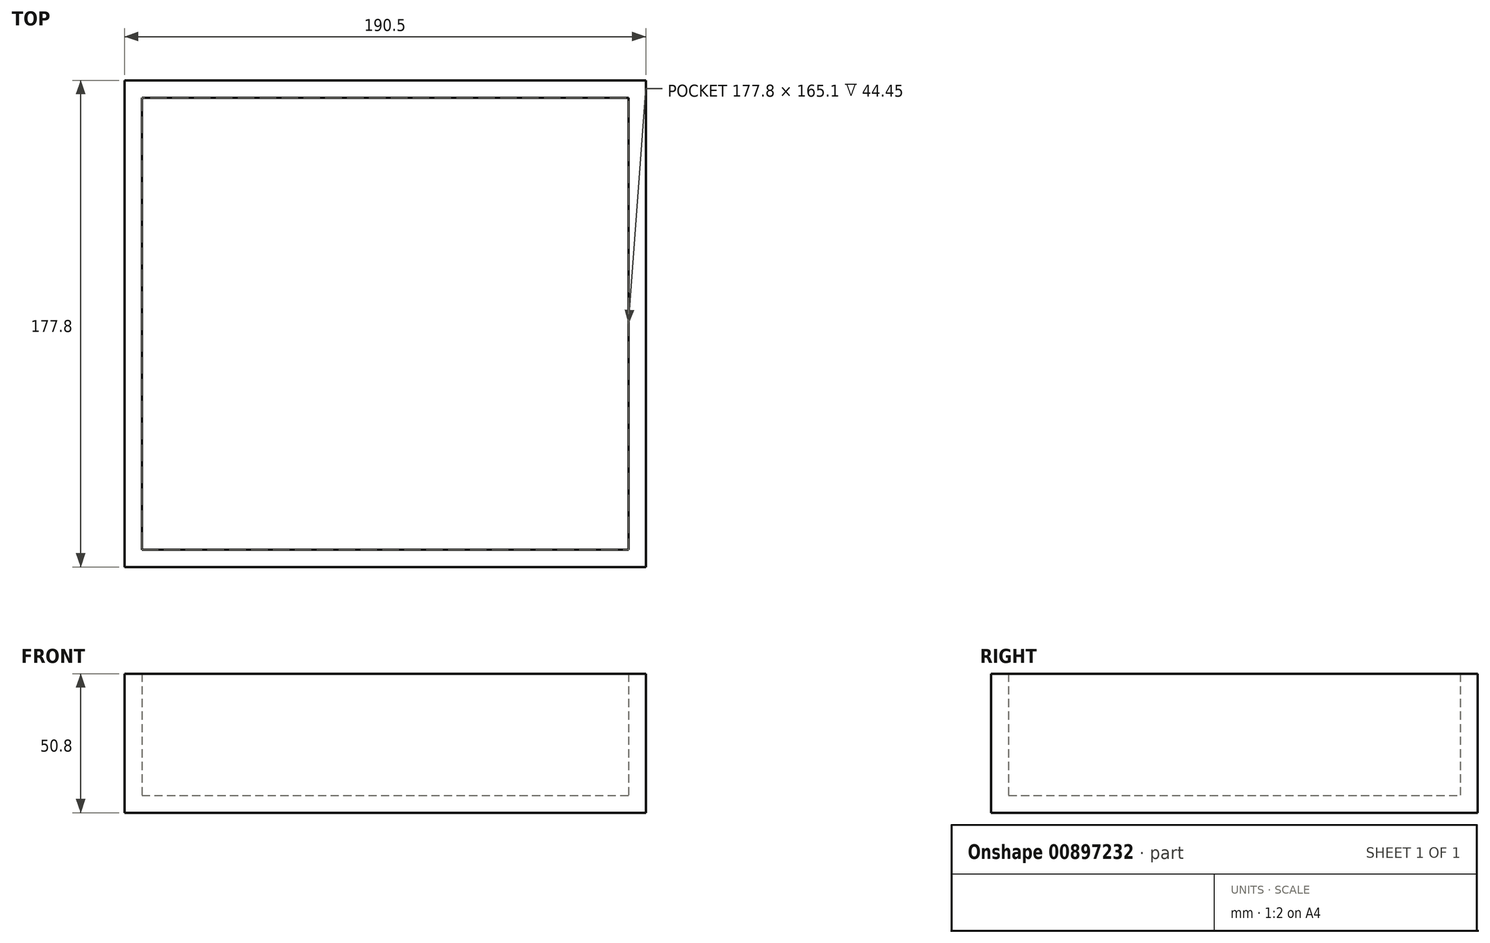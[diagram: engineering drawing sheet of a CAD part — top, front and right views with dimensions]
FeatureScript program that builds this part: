
annotation { "Feature Type Name" : "Feature", "Feature Type Description" : "" }
export const myFeature = defineFeature(function(context is Context, id is Id, definition is map)
    precondition{}
    {
        {
            var Q0;
            Q0=qCreatedBy(makeId("Top.planeOp"),FACE);
            var sketch = newSketch(context, id + "F0", { "sketchPlane" : qUnion([Q0])});
            skLineSegment(sketch, "E0.bottom", {"start": v(-88.9, -82.55) * mm, "end": v(88.9, -82.55) * mm});
            skLineSegment(sketch, "E0.top", {"start": v(-88.9, 82.55) * mm, "end": v(88.9, 82.55) * mm});
            skLineSegment(sketch, "E0.left", {"start": v(-88.9, -82.55) * mm, "end": v(-88.9, 82.55) * mm});
            skLineSegment(sketch, "E0.right", {"start": v(88.9, -82.55) * mm, "end": v(88.9, 82.55) * mm});
            skSolve(sketch);
        }
        {
            var Q0;
            Q0 = qSketchRegion(id + "F0", true);
            extrude(context, id + "F1", {"entities" : qUnion([Q0]), "depth" : 6.35 * mm, "offsetDistance" : 25.4 * mm});
        }
        {
            var Q0;
            Q0=qCreatedBy(makeId("Top.planeOp"),FACE);
            var sketch = newSketch(context, id + "F2", { "sketchPlane" : qUnion([Q0])});
            skLineSegment(sketch, "E1.bottom", {"start": v(-95.25, 88.9) * mm, "end": v(95.25, 88.9) * mm});
            skLineSegment(sketch, "E1.top", {"start": v(-95.25, -88.9) * mm, "end": v(95.25, -88.9) * mm});
            skLineSegment(sketch, "E1.left", {"start": v(-95.25, 88.9) * mm, "end": v(-95.25, -88.9) * mm});
            skLineSegment(sketch, "E1.right", {"start": v(95.25, 88.9) * mm, "end": v(95.25, -88.9) * mm});
            skLineSegment(sketch, "E2.bottom", {"start": v(-88.9, 82.55) * mm, "end": v(88.9, 82.55) * mm});
            skLineSegment(sketch, "E2.top", {"start": v(-88.9, -82.55) * mm, "end": v(88.9, -82.55) * mm});
            skLineSegment(sketch, "E2.left", {"start": v(-88.9, 82.55) * mm, "end": v(-88.9, -82.55) * mm});
            skLineSegment(sketch, "E2.right", {"start": v(88.9, 82.55) * mm, "end": v(88.9, -82.55) * mm});
            skSolve(sketch);
        }
        {
            var Q0;
            Q0 = qSketchRegion(id + "F2", true);
            extrude(context, id + "F3", {"entities" : qUnion([Q0]), "operationType" : NewBodyOperationType.ADD, "depth" : 50.8 * mm, "offsetDistance" : 25.4 * mm});
        }
    });
